# Revit family: FL4NX-EP_2014
name_source: partatom
category: Specialty Equipment
revit_build: Autodesk Revit 2014 (Build: 20130308_1515(x64)
units: mm (PartAtom-declared; Revit-internal decimal feet)

## types (2) — shared parameters
Back Clearance = 3"
Bumper = Extruded PVC - 733 Turquoise Blue
Case = Textured Sheet Metal (Steel Painted) - 149 White Satin Matte
Case Interior - Back Panel = Sheet Metal (Steel Painted) - 700 Interior White
Case Interior - Side Panel = Sheet Metal (Steel Painted) - 700 Interior White
Cutsheet URL = http://www.hussmann.com
Depth = 37"
Description = Floral, 4-Deck, Narrow Footprint, Extra High Energy Efficiency Coil
End Weight = 100.00 lbf
Ends = Textured Sheet Metal (Steel Painted) - 149 White Satin Matte
Height = 67 1/8"
Manufacturer = Hussmann Corporation
Manufacturer Disclaimer = The information in this file is not intended to be an exact representation of the corresponding Hussmann product.  Further, we reserve the right to change or revise specifications and product design in connection with any feature of our products. Such changes do not entitle the buyer to corresponding changes, improvements, additions, or replacements for equipment previously sold or shipped.
Model = FL4NX-EP
Model URL = http://www.hussmann.com
Note from Manufacturer = This model only comes in 8'-0" and 12'-0" lengths.
Number of Shelves = 3
Refrigeration Lines Liquid = 3/8"
Refrigeration Lines Suction = 7/8"
Revit Family Date = 09/30/2016
Shelves = Sheet Metal (Steel Painted) - 700 Interior White
Splashguard = Textured Sheet Metal (Steel Painted) - 701 Black
Top Clearance = 3"
Trim = Stainless Steel
Type Comments = Excel
URL = www.hussmann.com
Waste Drain = 1 1/4"
Waste Drain Location = 12 1/8"

## per-type parameters (varying)
| type | Case Weight | Number of Supports | Total Weight | Width |
| 12'-0" Length | 1500.00 lbf | 4 | 1700.00 lbf | 144 1/2" |
| 8'-0" Length | 1200.00 lbf | 3 | 1400.00 lbf | 96 3/8" |

## geometry (parser evidence)
native form markers: Blend x8, Sweep x13
no freeform markers — native parametric forms only
